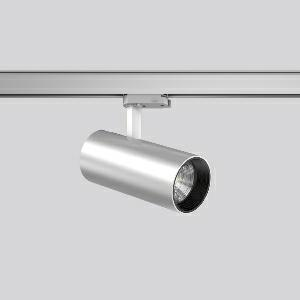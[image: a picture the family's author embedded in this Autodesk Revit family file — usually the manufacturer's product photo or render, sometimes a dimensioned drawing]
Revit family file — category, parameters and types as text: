
# Revit family: deecos_s_mini_742201_004_1_8d2a
name_source: partatom
category: Lighting Fixtures
units: mm (PartAtom-declared; Revit-internal decimal feet)

## family parameters
Cut with Voids When Loaded = No
Host = Face
Light Source = No
Part Type = Normal
Room Calculation Point = No
Round Connector Dimension = Use Diameter
Shared = No

## types (1)
- DEECOS S mini (1 x LED Modul 940, 2450 lm, 4000)
    Apparent Load = 20 VA
    Approval mark = CE
    CIE Flux Codes = 80 99 100 100 100
    Color Rendering = 92
    Color Temperature = 4000
    Default Elevation = 1800 mm
    Description = Series: DEECOS S mini
LED surface-mounted projector in modern design with no visible cooling ribs. Housing: die-cast aluminium, powder-coated. Rotation range: 356°. Swivel range: 90°. Black plastic ring and recessed LED to prevent glare from the side. Optical assembly with lens made of plastic (polycarbonate) for the best homogeneous light distribution - can be changed without tools. Best colour rendering index Ra>90. With multi adaptor for 3-circuit tracks 230 V. Suitable for Track on ceiling, Wall track. High quality converter without flickering and stroboscopic effect. The following accessories can be mounted without use of tools: interchangeable lenses, decorative glasses, honeycomb louvre, clear and frosted diffusers, white interchangeable plastic ring. 
Colour: silver
Diameter: 87 mm
Height: 214 mm
Lamp: LED
Socket: without socket
Colour temperature: 4000K
Colour rendering index (CRI): 92
System power: 20 W
Rated luminous flux: 2450 lm
Luminous efficiency: 123 lm/W
Control gear: Regulated power supply
Protection class: I
Type of protection: IP 20
    Height = 214 mm
    Lamp = 1 x LED Modul 940
    Lamp Light Flux = 2450 lm
    Lamp count = 1
    Length = 87 mm
    Lifetime = 50000 h
    Luminous efficacy = 123 lm/W
    Manufacturer = RZB
    ModVariant = No
    Model = 742201.004.1
    Mounting Place = Ceiling
    Mounting Type = Rail mounted
    Number of Poles = 1
    OnlyDefault = Yes
    Power Factor = 1
    Product Name = DEECOS S mini
    Product group = Track mounted projectors
    ProductGroupID = 301
    Protection Class = Protection class I
    Protection Degree = IP 20
    RLX_Detail_Level = 1
    RLX_Emergency_Light_Flux = 0 lm
    RLX_Emergency_Type = 0
    RLX_Emergency_Type_DB = No
    RlxData = <blob elided: 37637 chars, md5=96022bfe>
    Socket = socket
    Standby Power = 0 W
    System Light Flux = 2450 lm
    System Power = 20 W
    Type Comments = Product without accessories
    Type Image = 741930.004.jpg
    URL = http://relux.com
    VarID = ---
    Voltage = 230 V
    Voltage Range = 220-240 V
    Weight = 0.00 kg
    Width = 0 mm  [stored 0 ft]

note: [stored X ft] marks values corroborated as IEEE doubles in the binary element streams (Revit-internal decimal feet)

## geometry (parser evidence)
native form markers: Blend x4, Sweep x12
no freeform markers — native parametric forms only
